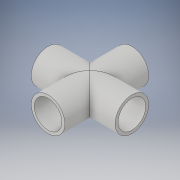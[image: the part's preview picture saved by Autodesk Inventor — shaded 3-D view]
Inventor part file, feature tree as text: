
AUTODESK INVENTOR PART (.ipt)
format: ipt  version: 2018 (Build 220112000, 112)  size: 162,304 bytes
history: native  units: in
note: dims shown in document units (in); Inventor stores cm internally (conversion verified against a paired STEP export)
features: sketch x10, extrude x8, plane x1
ambient origin geometry x8: Origin, YZ Plane, XZ Plane, XY Plane, X Axis, Y Axis, Z Axis, Center Point
bodies: Solid1 (feature_tree)
feature tree (19):
  extrude  "Extrusion1"  Depth=4.0in TaperAngle=0.0deg
  sketch  "Sketch2"  dims[d3=4.0in d4=0.0in d5=1.321in]
  sketch  "Sketch3"  dims[d6=1.321in d7=1.321in]
  plane  "Work Plane1"
  extrude  "Extrusion2"  Depth=4.0in
  sketch  "Sketch5"  dims[d11=1.25in d12=0.0in d13=1.25in d14=0.0in]
  sketch  "Sketch6"  dims[d15=1.25in d16=0.0in d17=1.0in]
  sketch  "Sketch7"  dims[d18=1.0in d19=4.0in d20=0.0in]
  sketch  "Sketch8"  dims[d21=4.0in d22=0.0in]
  extrude  "Extrusion3"  Depth=1.321in
  extrude  "Extrusion4"  Depth=1.25in TaperAngle=0.0deg
  extrude  "Extrusion5"  Depth=1.25in TaperAngle=0.0deg
  extrude  "Extrusion6"  Depth=1.25in
  sketch  "Sketch9"
  extrude  "Extrusion7"  Depth=4.0in TaperAngle=0.0deg
  extrude  "Extrusion8"  [1 undecoded]
  sketch  "Sketch1"  dims[d0=1.605in d1=4.0in d2=0.0in]
  sketch  "Sketch4"  dims[d8=1.321in d9=1.25in d10=0.0in]
  sketch  "Sketch10"
note: 1 required parameter value undecoded (feature->parameter linkage not recoverable at this tier; creation-order binding heuristic only, values carry confidence <= 0.55)
